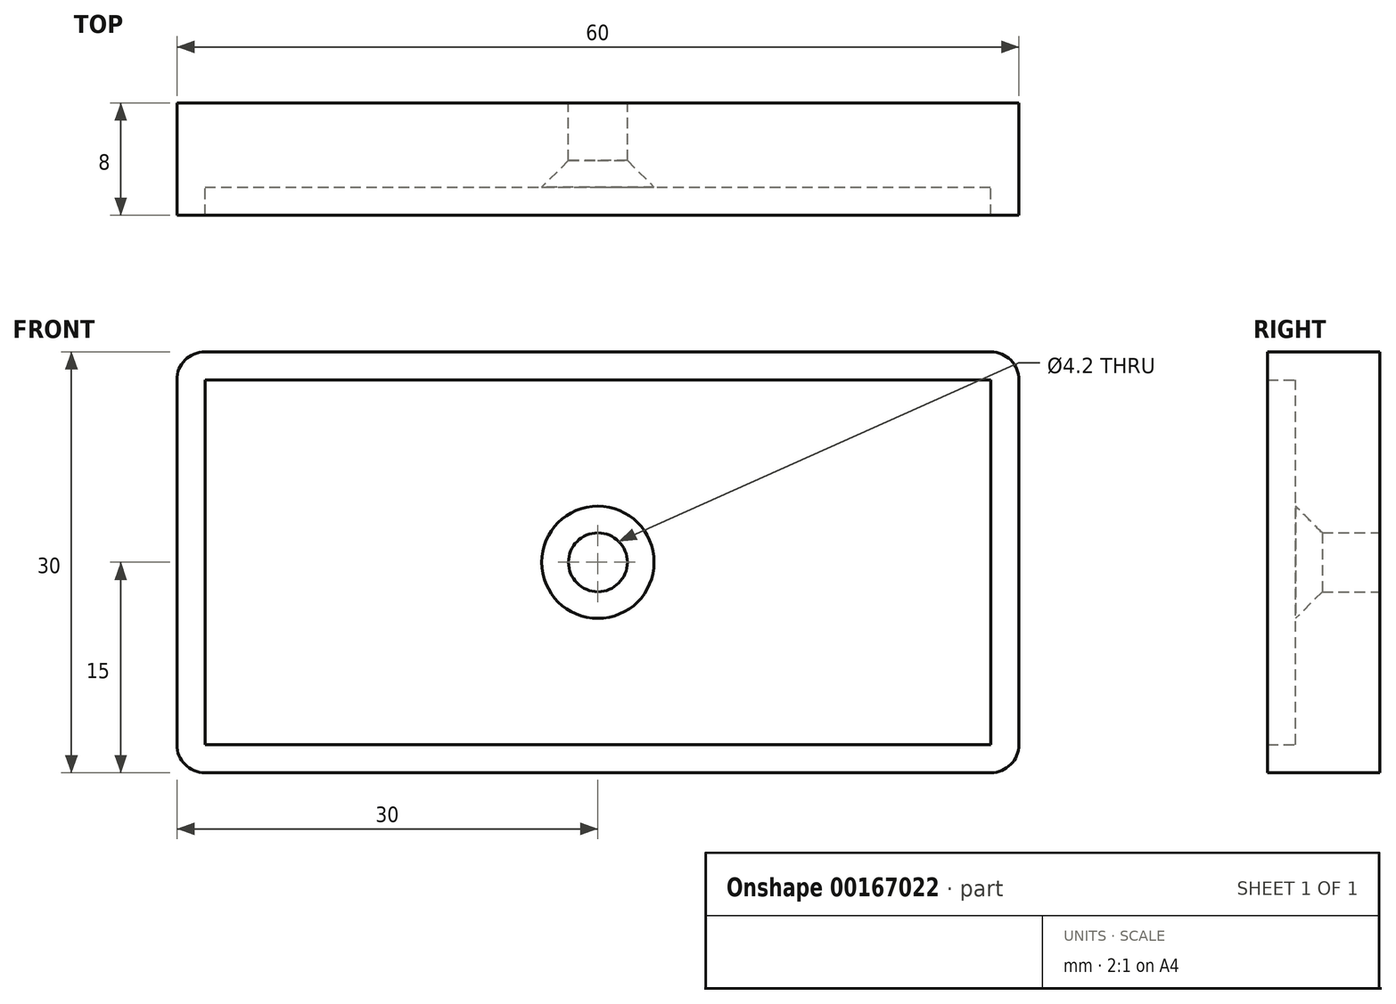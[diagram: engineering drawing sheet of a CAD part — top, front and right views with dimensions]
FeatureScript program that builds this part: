
annotation { "Feature Type Name" : "Feature", "Feature Type Description" : "" }
export const myFeature = defineFeature(function(context is Context, id is Id, definition is map)
    precondition{}
    {
        {
            var Q0;
            Q0=qCreatedBy(makeId("Front.planeOp"),FACE);
            var sketch = newSketch(context, id + "F0", { "sketchPlane" : qUnion([Q0])});
            skLineSegment(sketch, "E0", {"start": v(0, 0) * mm, "end": v(-60, 0) * mm});
            skLineSegment(sketch, "E1", {"start": v(-60, 0) * mm, "end": v(-60, 30) * mm});
            skLineSegment(sketch, "E2", {"start": v(-60, 30) * mm, "end": v(0, 30) * mm});
            skLineSegment(sketch, "E3", {"start": v(0, 30) * mm, "end": v(0, 0) * mm});
            skLineSegment(sketch, "E4.0", {"start": v(-58, 28) * mm, "end": v(-2, 28) * mm});
            skLineSegment(sketch, "E4.1", {"start": v(-58, 2) * mm, "end": v(-58, 28) * mm});
            skLineSegment(sketch, "E4.2", {"start": v(-2, 2) * mm, "end": v(-58, 2) * mm});
            skLineSegment(sketch, "E4.3", {"start": v(-2, 28) * mm, "end": v(-2, 2) * mm});
            skLineSegment(sketch, "E5", {"start": v(-60, 15) * mm, "end": v(-30, 15) * mm});
            skSolve(sketch);
        }
        {
            var Q0;
            Q0=qSketchRegion(id+"F0",true);
            var Q1;
            Q1=makeQuery(id+"F0.imprint","IMPRINT",FACE,{"disambiguationData":[TD([[makeQuery(id+"F0.imprint","IMPRINT",EDGE,{"derivedFrom":sQuery(id+"F0.wireOp",EDGE,"E4.0")}),-1.0]])]});
            extrude(context, id + "F1", {"entities" : qUnion([Q0, Q1]), "oppositeDirection" : true, "depth" : 6 * mm, "offsetDistance" : 25 * mm});
        }
        {
            var Q0;
            Q0=makeQuery(id+"F0.imprint","IMPRINT",FACE,{"disambiguationData":[TD([[makeQuery(id+"F0.imprint","IMPRINT",EDGE,{"derivedFrom":sQuery(id+"F0.wireOp",EDGE,"E0")}),-1.0]])]});
            extrude(context, id + "F2", {"entities" : qUnion([Q0]), "operationType" : NewBodyOperationType.ADD, "depth" : 2 * mm, "offsetDistance" : 25 * mm});
        }
        {
            var Q0;
            Q0=sQuery(id+"F0.wireOp",VERTEX,"E5.end");
            var Q1;
            Q1=makeQuery(id+"F1.opExtrude","SWEPT_BODY",BODY,{"disambiguationData":[OSD([sQuery(id+"F0.wireOp",EDGE,"E0"),sQuery(id+"F0.wireOp",EDGE,"E1"),sQuery(id+"F0.wireOp",EDGE,"E2"),sQuery(id+"F0.wireOp",EDGE,"E3")])]});
            hole(context, id + "F3", {"style" : HoleStyle.C_SINK, "endStyle" : HoleEndStyle.BLIND, "holeDiameter" : 4.2 * mm, "cSinkDiameter" : 8 * mm, "cSinkAngle" : 90 * degree, "majorDiameter" : 5 * mm, "holeDepth" : 15 * mm, "isTappedThrough" : true, "tappedDepth" : 12 * mm, "tapClearance" : 3, "locations" : qUnion([Q0]), "scope" : qUnion([Q1]), "startStyle" : HoleStartStyle.PART});
        }
        {
            var Q0;
            {var subQ0=sQuery(id+"F0.wireOp",EDGE,"E2");var subQ1=sQuery(id+"F0.wireOp",EDGE,"E1");Q0=makeQuery(id+"F2.boolean.opBoolean","MERGE",EDGE,{"derivedFrom":[makeQuery(id+"F1.opExtrude","SWEPT_EDGE",EDGE,{"disambiguationData":[OSD([subQ1,subQ0])]}),makeQuery(id+"F2.opExtrude","SWEPT_EDGE",EDGE,{"disambiguationData":[OSD([subQ1,subQ0])]})]});}
            var Q1;
            {var subQ0=sQuery(id+"F0.wireOp",EDGE,"E3");var subQ1=sQuery(id+"F0.wireOp",EDGE,"E2");Q1=makeQuery(id+"F2.boolean.opBoolean","MERGE",EDGE,{"derivedFrom":[makeQuery(id+"F1.opExtrude","SWEPT_EDGE",EDGE,{"disambiguationData":[OSD([subQ1,subQ0])]}),makeQuery(id+"F2.opExtrude","SWEPT_EDGE",EDGE,{"disambiguationData":[OSD([subQ1,subQ0])]})]});}
            var Q2;
            {var subQ0=sQuery(id+"F0.wireOp",EDGE,"E3");var subQ1=sQuery(id+"F0.wireOp",EDGE,"E0");Q2=makeQuery(id+"F2.boolean.opBoolean","MERGE",EDGE,{"derivedFrom":[makeQuery(id+"F1.opExtrude","SWEPT_EDGE",EDGE,{"disambiguationData":[OSD([subQ1,subQ0])]}),makeQuery(id+"F2.opExtrude","SWEPT_EDGE",EDGE,{"disambiguationData":[OSD([subQ1,subQ0])]})]});}
            var Q3;
            {var subQ0=sQuery(id+"F0.wireOp",EDGE,"E1");var subQ1=sQuery(id+"F0.wireOp",EDGE,"E0");Q3=makeQuery(id+"F2.boolean.opBoolean","MERGE",EDGE,{"derivedFrom":[makeQuery(id+"F1.opExtrude","SWEPT_EDGE",EDGE,{"disambiguationData":[OSD([subQ1,subQ0])]}),makeQuery(id+"F2.opExtrude","SWEPT_EDGE",EDGE,{"disambiguationData":[OSD([subQ1,subQ0])]})]});}
            fillet(context, id + "F4", {"entities" : qUnion([Q0, Q1, Q2, Q3]), "radius" : 2 * mm, "tangentPropagation" : true, "allowEdgeOverflow" : false});
        }
    });
